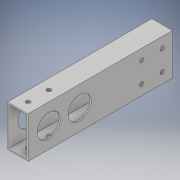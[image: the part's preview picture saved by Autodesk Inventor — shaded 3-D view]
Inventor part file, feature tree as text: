
AUTODESK INVENTOR PART (.ipt)
format: ipt  version: 2018 (Build 220112000, 112)  size: 164,352 bytes
history: native  units: in
note: dims shown in document units (in); Inventor stores cm internally (conversion verified against a paired STEP export)
features: extrude x2, hole x2, sketch x2, shell x1
ambient origin geometry x8: Origin, YZ Plane, XZ Plane, XY Plane, X Axis, Y Axis, Z Axis, Center Point
bodies: Solid1 (feature_tree)
feature tree (7):
  extrude  "Extrusion1"  Depth=7.0in
  shell  "Shell1"  Thickness=1.0in
  extrude  "Extrusion2"  Depth=1.0in
  hole  "Hole1"  [1 undecoded]
  hole  "Hole2"  [1 undecoded]
  sketch  "Sketch1"  dims[d0=2.0in d1=7.0in d2=1.0in d3=0.0in]
  sketch  "Sketch2"  dims[d4=0.0625in d5=1.0in d6=1.125in d7=1.5in d8=1.125in d9=1.5in d10=1.5in d11=0.5in d12=0.5in d13=0.5in d14=0.5in d15=0.5in d16=0.5in d17=0.5in d18=0.5in d19=1.5in d20=1.5in d21=0.2031in d22=0.2031in d23=0.2031in d24=0.2031in d25=2.0in d26=0.0in d27=0.5in d28=0.5in d29=0.2031in d30=0.75in d31=0.375in d32=0.25in d33=0.5635in d34=1.0in d35=0.8108in d36=0.5in d37=1.5in d38=0.2031in d39=0.75in d40=0.375in d41=0.25in d42=0.5635in d43=1.0in d44=0.8108in]
note: 2 required parameter values undecoded (feature->parameter linkage not recoverable at this tier; creation-order binding heuristic only, values carry confidence <= 0.55)
